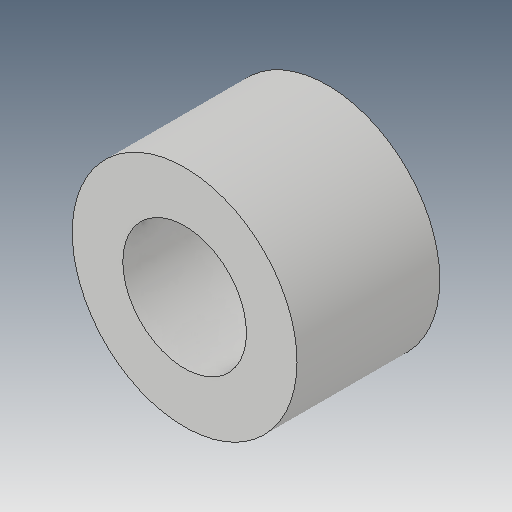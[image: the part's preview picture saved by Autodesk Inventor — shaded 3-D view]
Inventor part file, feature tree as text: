
AUTODESK INVENTOR PART (.ipt)
format: ipt  version: 2017 (Build 210142000, 142)  size: 101,376 bytes
history: native  units: mm
features: other x4, extrude x1, sketch x1, reference x1
ambient origin geometry x8: Origin, YZ Plane, XZ Plane, XY Plane, X Axis, Y Axis, Z Axis, Center Point
bodies: Solid1 (feature_tree)
feature tree (7):
  extrude  "Extrusion1"  Depth=10.0mm
  sketch  "Sketch1"  dims[d0=5.5mm d1=10.0mm d2=6.35mm d3=0.0mm]
  reference  "Reference1"
  parser-record x1  (decoder bookkeeping rows leaked as tree rows — omitted from the tree; the rows remain in map.json)
  other  "DelrinY-Wheel-Top.iam"
  other  "Delrin Wheel:1"
  other  "SKF 625:1"
note: 1 file-system path scrubbed to <path> (originals preserved in map.json)
